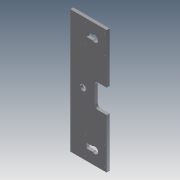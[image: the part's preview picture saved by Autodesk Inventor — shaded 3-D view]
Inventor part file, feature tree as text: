
AUTODESK INVENTOR PART (.ipt)
format: ipt  version: 2011 (Build 150239000, 239)  size: 458,752 bytes
history: native  units: in
note: dims shown in document units (in); Inventor stores cm internally (conversion verified against a paired STEP export)
features: extrude x43, sketch x43, fillet x2
ambient origin geometry x8: Origin, YZ Plane, XZ Plane, XY Plane, X Axis, Y Axis, Z Axis, Center Point
bodies: Solid1 (feature_tree)
feature tree (88):
  extrude  "Extrusion1"  Depth=4.0in
  extrude  "Extrusion2"  Depth=2.16in
  extrude  "Extrusion3"  Depth=1.7655in
  extrude  "Extrusion4"  Depth=0.029in TaperAngle=0.0deg
  extrude  "Extrusion5"  Depth=2.36in
  fillet  "Fillet1"  Radius=2.56in
  extrude  "Extrusion6"  Depth=0.125in
  extrude  "Extrusion7"  Depth=0.262in TaperAngle=0.0deg
  extrude  "Extrusion8"  Depth=0.029in TaperAngle=0.0deg
  extrude  "Extrusion9"  Depth=0.156in
  extrude  "Extrusion10"  Depth=0.5in TaperAngle=0.0deg
  extrude  "Extrusion11"  Depth=0.5in TaperAngle=0.0deg
  extrude  "Extrusion12"  Depth=1.875in TaperAngle=0.0deg
  extrude  "Extrusion13"  Depth=2.125in TaperAngle=0.0deg
  sketch  "Sketch14"  dims[d44=2.125in d45=0.0in d46=2.125in d47=0.0in]
  sketch  "Sketch15"  dims[d48=2.125in d49=0.0in d50=1.875in d51=0.0in]
  sketch  "Sketch16"  dims[d52=2.125in d53=0.0in d54=2.125in d55=0.0in]
  sketch  "Sketch17"  dims[d56=1.875in d57=0.0in d58=1.875in d59=0.0in]
  extrude  "Extrusion14"  Depth=2.125in TaperAngle=0.0deg
  extrude  "Extrusion15"  Depth=1.875in TaperAngle=0.0deg
  extrude  "Extrusion16"  Depth=2.125in TaperAngle=0.0deg
  extrude  "Extrusion17"  Depth=1.875in TaperAngle=0.0deg
  extrude  "Extrusion18"  Depth=2.125in TaperAngle=0.0deg
  extrude  "Extrusion19"  Depth=6.248in TaperAngle=0.0deg
  extrude  "Extrusion20"  Depth=1.281in
  extrude  "Extrusion21"  Depth=7.0in TaperAngle=0.0deg
  extrude  "Extrusion22"  Depth=2.0in
  extrude  "Extrusion23"  Depth=4.0in
  extrude  "Extrusion24"  Depth=2.0in
  extrude  "Extrusion25"  Depth=1.0in TaperAngle=0.0deg
  extrude  "Extrusion26"  Depth=0.25in
  extrude  "Extrusion27"  Depth=0.25in TaperAngle=0.0deg
  extrude  "Extrusion28"  Depth=0.25in TaperAngle=0.0deg
  extrude  "Extrusion29"  Depth=0.875in
  extrude  "Extrusion30"  Depth=0.5in TaperAngle=0.0deg
  extrude  "Extrusion31"  Depth=0.875in
  extrude  "Extrusion32"  Depth=0.5in TaperAngle=0.0deg
  extrude  "Extrusion33"  Depth=0.4134in
  extrude  "Extrusion34"  Depth=0.8268in
  fillet  "Fillet2"  Radius=0.4134in
  extrude  "Extrusion35"  Depth=0.8268in
  extrude  "Extrusion36"  Depth=0.5315in
  extrude  "Extrusion37"  Depth=0.6299in
  extrude  "Extrusion38"  Depth=0.6299in
  extrude  "Extrusion39"  Depth=0.5709in
  extrude  "Extrusion40"  Depth=1.063in
  extrude  "Extrusion41"  Depth=0.0787in
  extrude  "Extrusion42"  [1 undecoded]
  extrude  "Extrusion43"  [1 undecoded]
  sketch  "Sketch1"  dims[d0=4.0in d1=4.0in]
  sketch  "Sketch2"  dims[d2=0.029in d3=0.0in d4=2.16in]
  sketch  "Sketch3"  dims[d5=0.029in d6=0.0in d7=1.7655in]
  sketch  "Sketch4"  dims[d8=0.156in d9=0.029in d10=0.0in]
  sketch  "Sketch5"  dims[d11=0.029in d12=0.0in d13=2.36in d14=2.56in]
  sketch  "Sketch6"  dims[d15=0.262in d16=0.0in d17=0.125in]
  sketch  "Sketch7"  dims[d18=0.362in d19=0.0in d20=0.262in d21=0.0in]
  sketch  "Sketch8"  dims[d22=0.1in d23=0.0in d24=0.029in d25=0.0in]
  sketch  "Sketch9"  dims[d26=1.594in d27=0.156in]
  sketch  "Sketch10"  dims[d28=0.029in d29=0.0in d30=0.5in d31=0.0in]
  sketch  "Sketch11"  dims[d32=0.75in d33=0.0in d34=0.5in d35=0.0in]
  sketch  "Sketch12"  dims[d36=2.125in d37=0.0in d38=1.875in d39=0.0in]
  sketch  "Sketch13"  dims[d40=1.875in d41=0.0in d42=2.125in d43=0.0in]
  sketch  "Sketch18"  dims[d60=2.125in d61=0.0in d62=2.125in d63=0.0in]
  sketch  "Sketch19"  dims[d64=0.875in d65=0.0in d66=6.248in d67=0.0in]
  sketch  "Sketch20"  dims[d68=7.0in d69=0.0in d70=1.281in]
  sketch  "Sketch21"  dims[d71=3.188in d72=7.0in d73=0.0in]
  sketch  "Sketch22"  dims[d74=0.25in d75=0.0in d76=2.0in]
  sketch  "Sketch23"  dims[d77=2.0in d78=4.0in]
  sketch  "Sketch24"  dims[d79=1.0in d80=0.0in d81=2.0in]
  sketch  "Sketch25"  dims[d82=1.0in d83=1.0in d84=0.0in]
  sketch  "Sketch26"  dims[d85=0.5in d86=0.25in]
  sketch  "Sketch27"  dims[d87=0.25in d88=0.25in d89=0.0in]
  sketch  "Sketch28"  dims[d90=0.25in d91=0.0in d92=0.25in d93=0.0in]
  sketch  "Sketch29"  dims[d94=0.656in d95=0.875in]
  sketch  "Sketch30"  dims[d96=0.5in d97=0.0in d98=0.5in d99=0.0in]
  sketch  "Sketch31"  dims[d100=0.875in d101=0.875in]
  sketch  "Sketch32"  dims[d102=0.5in d103=0.0in d104=0.5in d105=0.0in]
  sketch  "Sketch33"  dims[d106=1.1024in d107=0.4134in]
  sketch  "Sketch34"  dims[d108=1.378in d109=0.8268in d110=0.4134in]
  sketch  "Sketch35"  dims[d111=1.378in d112=0.8268in]
  sketch  "Sketch36"  dims[d113=1.0in d114=0.0in d115=0.5315in]
  sketch  "Sketch37"  dims[d116=0.5709in d117=0.6299in]
  sketch  "Sketch38"  dims[d118=1.063in d119=0.6299in]
  sketch  "Sketch39"  dims[d120=0.5315in d121=0.5709in]
  sketch  "Sketch40"  dims[d122=0.6299in d123=1.063in]
  sketch  "Sketch41"  dims[d124=0.6299in d125=0.0787in]
  sketch  "Sketch42"  dims[d126=1.0in d127=0.0in]
  sketch  "Sketch43"
note: 2 required parameter values undecoded (feature->parameter linkage not recoverable at this tier; creation-order binding heuristic only, values carry confidence <= 0.55)
